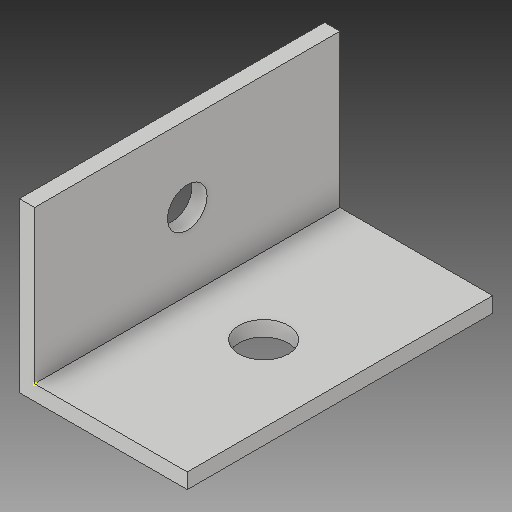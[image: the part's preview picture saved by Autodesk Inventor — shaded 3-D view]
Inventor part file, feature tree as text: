
AUTODESK INVENTOR PART (.ipt)
format: ipt  version: 2018 (Build 220112000, 112)  size: 114,688 bytes
history: native  units: in
note: dims shown in document units (in); Inventor stores cm internally (conversion verified against a paired STEP export)
features: sketch x5, hole x2, extrude x1
ambient origin geometry x8: Origin, YZ Plane, XZ Plane, XY Plane, X Axis, Y Axis, Z Axis, Center Point
bodies: Solid1 (feature_tree)
feature tree (8):
  sketch  "Sketch1"  dims[d0=0.7874in d1=0.0787in]
  extrude  "Extrusion1"  Depth=0.0787in
  sketch  "Sketch3"  dims[d4=0.0787in d5=0.7874in]
  hole  "Hole1"  [1 undecoded]
  hole  "Hole2"  [1 undecoded]
  sketch  "Sketch2"  dims[d2=0.8661in d3=0.8661in]
  sketch  "Sketch4"  dims[d6=1.5748in d7=0.0in]
  sketch  "Sketch5"  dims[d9=0.2559in d10=0.2559in d11=0.2953in d12=0.1189in d13=0.0984in d14=0.5635in d15=0.3937in d16=0.8108in d17=0.2047in d18=0.2047in d19=0.2953in d20=0.1189in d21=0.0984in d22=0.5635in d23=0.3937in d24=0.8108in]
note: 2 required parameter values undecoded (feature->parameter linkage not recoverable at this tier; creation-order binding heuristic only, values carry confidence <= 0.55)
